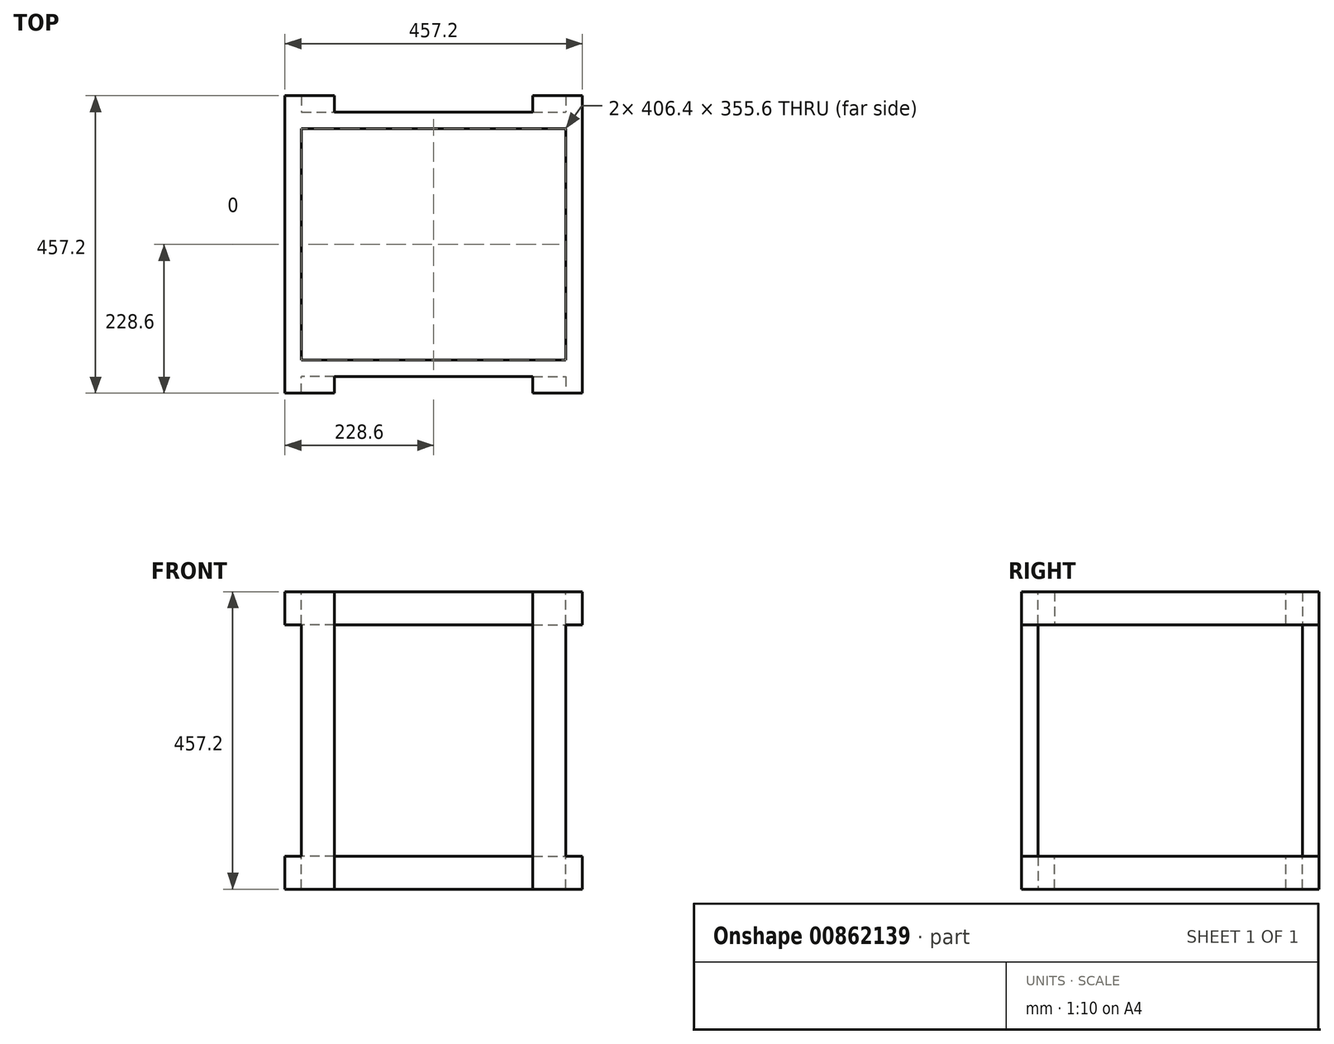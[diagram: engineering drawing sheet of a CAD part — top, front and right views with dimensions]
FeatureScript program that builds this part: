
annotation { "Feature Type Name" : "Feature", "Feature Type Description" : "" }
export const myFeature = defineFeature(function(context is Context, id is Id, definition is map)
    precondition{}
    {
        {
            var Q0;
            Q0=qCreatedBy(makeId("Front.planeOp"),FACE);
            var sketch = newSketch(context, id + "F0", { "sketchPlane" : qUnion([Q0])});
            skLineSegment(sketch, "E0.bottom", {"start": v(0, 0) * mm, "end": v(50.8, 0) * mm});
            skLineSegment(sketch, "E0.top", {"start": v(0, 457.2) * mm, "end": v(50.8, 457.2) * mm});
            skLineSegment(sketch, "E0.left", {"start": v(0, 0) * mm, "end": v(0, 457.2) * mm});
            skLineSegment(sketch, "E0.right", {"start": v(50.8, 0) * mm, "end": v(50.8, 457.2) * mm});
            skSolve(sketch);
        }
        {
            var Q0;
            Q0=makeQuery(id+"F0.imprint","IMPRINT",FACE,{"disambiguationData":[TD([[makeQuery(id+"F0.imprint","IMPRINT",EDGE,{"derivedFrom":sQuery(id+"F0.wireOp",EDGE,"E0.bottom")}),1.0]])]});
            extrude(context, id + "F1", {"entities" : qUnion([Q0]), "depth" : 25.4 * mm, "offsetDistance" : 25.4 * mm});
        }
        {
            var Q0;
            Q0=makeQuery(id+"F1.opExtrude","SWEPT_FACE",FACE,{"disambiguationData":[OSD([sQuery(id+"F0.wireOp",EDGE,"E0.right")])]});
            var sketch = newSketch(context, id + "F2", { "sketchPlane" : qUnion([Q0])});
            skLineSegment(sketch, "E1.bottom", {"start": v(-25.4, 457.2) * mm, "end": v(0, 457.2) * mm});
            skLineSegment(sketch, "E1.top", {"start": v(-25.4, 406.4) * mm, "end": v(0, 406.4) * mm});
            skLineSegment(sketch, "E1.left", {"start": v(-25.4, 457.2) * mm, "end": v(-25.4, 406.4) * mm});
            skLineSegment(sketch, "E1.right", {"start": v(0, 457.2) * mm, "end": v(0, 406.4) * mm});
            skSolve(sketch);
        }
        {
            var Q0;
            Q0=makeQuery(id+"F2.imprint","IMPRINT",FACE,{"disambiguationData":[TD([[makeQuery(id+"F2.imprint","IMPRINT",EDGE,{"derivedFrom":sQuery(id+"F2.wireOp",EDGE,"E1.bottom")}),-1.0]])]});
            extrude(context, id + "F3", {"entities" : qUnion([Q0]), "operationType" : NewBodyOperationType.ADD, "depth" : 25.4 * mm, "offsetDistance" : 25.4 * mm});
        }
        {
            var Q0;
            Q0=makeQuery(id+"F3.boolean.opBoolean","MERGE",FACE,{"derivedFrom":[makeQuery(id+"F1.opExtrude","CAP_FACE",FACE,{"disambiguationData":[OSD([sQuery(id+"F0.wireOp",EDGE,"E0.bottom"),sQuery(id+"F0.wireOp",EDGE,"E0.top"),sQuery(id+"F0.wireOp",EDGE,"E0.left"),sQuery(id+"F0.wireOp",EDGE,"E0.right")])],"isStart":false}),makeQuery(id+"F3.opExtrude","SWEPT_FACE",FACE,{"disambiguationData":[OSD([sQuery(id+"F2.wireOp",EDGE,"E1.left")])]})]});
            var sketch = newSketch(context, id + "F4", { "sketchPlane" : qUnion([Q0])});
            skLineSegment(sketch, "E2.bottom", {"start": v(76.2, 457.2) * mm, "end": v(50.8, 457.2) * mm});
            skLineSegment(sketch, "E2.top", {"start": v(76.2, 406.4) * mm, "end": v(50.8, 406.4) * mm});
            skLineSegment(sketch, "E2.left", {"start": v(76.2, 457.2) * mm, "end": v(76.2, 406.4) * mm});
            skLineSegment(sketch, "E2.right", {"start": v(50.8, 457.2) * mm, "end": v(50.8, 406.4) * mm});
            skSolve(sketch);
        }
        {
            var Q0;
            Q0=makeQuery(id+"F4.imprint","IMPRINT",FACE,{"disambiguationData":[TD([[makeQuery(id+"F4.imprint","IMPRINT",EDGE,{"derivedFrom":sQuery(id+"F4.wireOp",EDGE,"E2.bottom")}),-1.0]])]});
            extrude(context, id + "F5", {"entities" : qUnion([Q0]), "operationType" : NewBodyOperationType.ADD, "depth" : 431.8 * mm, "offsetDistance" : 25.4 * mm});
        }
        {
            var Q0;
            Q0=makeQuery(id+"F5.opExtrude","SWEPT_FACE",FACE,{"disambiguationData":[OSD([sQuery(id+"F4.wireOp",EDGE,"E2.right")])]});
            var sketch = newSketch(context, id + "F6", { "sketchPlane" : qUnion([Q0])});
            skLineSegment(sketch, "E3.bottom", {"start": v(457.2, 457.2) * mm, "end": v(431.8, 457.2) * mm});
            skLineSegment(sketch, "E3.top", {"start": v(457.2, 406.4) * mm, "end": v(431.8, 406.4) * mm});
            skLineSegment(sketch, "E3.left", {"start": v(457.2, 457.2) * mm, "end": v(457.2, 406.4) * mm});
            skLineSegment(sketch, "E3.right", {"start": v(431.8, 457.2) * mm, "end": v(431.8, 406.4) * mm});
            skSolve(sketch);
        }
        {
            var Q0;
            Q0=makeQuery(id+"F6.imprint","IMPRINT",FACE,{"disambiguationData":[TD([[makeQuery(id+"F6.imprint","IMPRINT",EDGE,{"derivedFrom":sQuery(id+"F6.wireOp",EDGE,"E3.bottom")}),1.0]])]});
            extrude(context, id + "F7", {"entities" : qUnion([Q0]), "operationType" : NewBodyOperationType.ADD, "depth" : 50.8 * mm, "offsetDistance" : 25.4 * mm});
        }
        {
            var Q0;
            Q0=makeQuery(id+"F7.boolean.opBoolean","MERGE",FACE,{"derivedFrom":[makeQuery(id+"F5.boolean.opBoolean","MERGE",FACE,{"derivedFrom":[makeQuery(id+"F3.opExtrude","SWEPT_FACE",FACE,{"disambiguationData":[OSD([sQuery(id+"F2.wireOp",EDGE,"E1.top")])]}),makeQuery(id+"F5.opExtrude","SWEPT_FACE",FACE,{"disambiguationData":[OSD([sQuery(id+"F4.wireOp",EDGE,"E2.top")])]})]}),makeQuery(id+"F7.opExtrude","SWEPT_FACE",FACE,{"disambiguationData":[OSD([sQuery(id+"F6.wireOp",EDGE,"E3.top")])]})]});
            var sketch = newSketch(context, id + "F8", { "sketchPlane" : qUnion([Q0])});
            skLineSegment(sketch, "E4.bottom", {"start": v(0, 431.8) * mm, "end": v(50.8, 431.8) * mm});
            skLineSegment(sketch, "E4.top", {"start": v(0, 457.2) * mm, "end": v(50.8, 457.2) * mm});
            skLineSegment(sketch, "E4.left", {"start": v(0, 431.8) * mm, "end": v(0, 457.2) * mm});
            skLineSegment(sketch, "E4.right", {"start": v(50.8, 431.8) * mm, "end": v(50.8, 457.2) * mm});
            skSolve(sketch);
        }
        {
            var Q0;
            Q0=makeQuery(id+"F8.imprint","IMPRINT",FACE,{"disambiguationData":[TD([[makeQuery(id+"F8.imprint","IMPRINT",EDGE,{"derivedFrom":sQuery(id+"F8.wireOp",EDGE,"E4.bottom")}),1.0]])]});
            extrude(context, id + "F9", {"entities" : qUnion([Q0]), "operationType" : NewBodyOperationType.ADD, "depth" : 406.4 * mm, "offsetDistance" : 25.4 * mm});
        }
        {
            var Q0;
            Q0=makeQuery(id+"F1.opExtrude","SWEPT_FACE",FACE,{"disambiguationData":[OSD([sQuery(id+"F0.wireOp",EDGE,"E0.right")])]});
            var sketch = newSketch(context, id + "F10", { "sketchPlane" : qUnion([Q0])});
            skLineSegment(sketch, "E5.bottom", {"start": v(0, 0) * mm, "end": v(-25.4, 0) * mm});
            skLineSegment(sketch, "E5.top", {"start": v(0, 50.8) * mm, "end": v(-25.4, 50.8) * mm});
            skLineSegment(sketch, "E5.left", {"start": v(0, 0) * mm, "end": v(0, 50.8) * mm});
            skLineSegment(sketch, "E5.right", {"start": v(-25.4, 0) * mm, "end": v(-25.4, 50.8) * mm});
            skSolve(sketch);
        }
        {
            var Q0;
            Q0=makeQuery(id+"F10.imprint","IMPRINT",FACE,{"disambiguationData":[TD([[makeQuery(id+"F10.imprint","IMPRINT",EDGE,{"derivedFrom":sQuery(id+"F10.wireOp",EDGE,"E5.bottom")}),1.0]])]});
            extrude(context, id + "F11", {"entities" : qUnion([Q0]), "operationType" : NewBodyOperationType.ADD, "depth" : 25.4 * mm, "offsetDistance" : 25.4 * mm});
        }
        {
            var Q0;
            Q0=makeQuery(id+"F11.boolean.opBoolean","MERGE",FACE,{"derivedFrom":[makeQuery(id+"F3.boolean.opBoolean","MERGE",FACE,{"derivedFrom":[makeQuery(id+"F1.opExtrude","CAP_FACE",FACE,{"disambiguationData":[OSD([sQuery(id+"F0.wireOp",EDGE,"E0.bottom"),sQuery(id+"F0.wireOp",EDGE,"E0.top"),sQuery(id+"F0.wireOp",EDGE,"E0.left"),sQuery(id+"F0.wireOp",EDGE,"E0.right")])],"isStart":false}),makeQuery(id+"F3.opExtrude","SWEPT_FACE",FACE,{"disambiguationData":[OSD([sQuery(id+"F2.wireOp",EDGE,"E1.left")])]})]}),makeQuery(id+"F11.opExtrude","SWEPT_FACE",FACE,{"disambiguationData":[OSD([sQuery(id+"F10.wireOp",EDGE,"E5.right")])]})]});
            var sketch = newSketch(context, id + "F12", { "sketchPlane" : qUnion([Q0])});
            skLineSegment(sketch, "E6.bottom", {"start": v(76.2, 0) * mm, "end": v(50.8, 0) * mm});
            skLineSegment(sketch, "E6.top", {"start": v(76.2, 50.8) * mm, "end": v(50.8, 50.8) * mm});
            skLineSegment(sketch, "E6.left", {"start": v(76.2, 0) * mm, "end": v(76.2, 50.8) * mm});
            skLineSegment(sketch, "E6.right", {"start": v(50.8, 0) * mm, "end": v(50.8, 50.8) * mm});
            skSolve(sketch);
        }
        {
            var Q0;
            Q0=makeQuery(id+"F12.imprint","IMPRINT",FACE,{"disambiguationData":[TD([[makeQuery(id+"F12.imprint","IMPRINT",EDGE,{"derivedFrom":sQuery(id+"F12.wireOp",EDGE,"E6.bottom")}),1.0]])]});
            extrude(context, id + "F13", {"entities" : qUnion([Q0]), "operationType" : NewBodyOperationType.ADD, "depth" : 431.8 * mm, "offsetDistance" : 25.4 * mm});
        }
        {
            var Q0;
            Q0=makeQuery(id+"F9.boolean.opBoolean","MERGE",FACE,{"derivedFrom":[makeQuery(id+"F7.opExtrude","SWEPT_FACE",FACE,{"disambiguationData":[OSD([sQuery(id+"F6.wireOp",EDGE,"E3.right")])]}),makeQuery(id+"F9.opExtrude","SWEPT_FACE",FACE,{"disambiguationData":[OSD([sQuery(id+"F8.wireOp",EDGE,"E4.bottom")])]})]});
            var sketch = newSketch(context, id + "F14", { "sketchPlane" : qUnion([Q0])});
            skLineSegment(sketch, "E7.bottom", {"start": v(-50.8, 457.2) * mm, "end": v(0, 457.2) * mm});
            skLineSegment(sketch, "E7.top", {"start": v(-50.8, 406.4) * mm, "end": v(0, 406.4) * mm});
            skLineSegment(sketch, "E7.left", {"start": v(-50.8, 457.2) * mm, "end": v(-50.8, 406.4) * mm});
            skLineSegment(sketch, "E7.right", {"start": v(0, 457.2) * mm, "end": v(0, 406.4) * mm});
            skSolve(sketch);
        }
        {
            var Q0;
            Q0=makeQuery(id+"F14.imprint","IMPRINT",FACE,{"disambiguationData":[TD([[makeQuery(id+"F14.imprint","IMPRINT",EDGE,{"derivedFrom":sQuery(id+"F14.wireOp",EDGE,"E7.bottom")}),1.0]])]});
            extrude(context, id + "F15", {"entities" : qUnion([Q0]), "operationType" : NewBodyOperationType.ADD, "depth" : 25.4 * mm, "offsetDistance" : 25.4 * mm});
        }
        {
            var Q0;
            Q0=makeQuery(id+"F15.boolean.opBoolean","MERGE",FACE,{"derivedFrom":[makeQuery(id+"F9.boolean.opBoolean","MERGE",FACE,{"derivedFrom":[makeQuery(id+"F7.opExtrude","CAP_FACE",FACE,{"disambiguationData":[OSD([sQuery(id+"F6.wireOp",EDGE,"E3.bottom"),sQuery(id+"F6.wireOp",EDGE,"E3.top"),sQuery(id+"F6.wireOp",EDGE,"E3.left"),sQuery(id+"F6.wireOp",EDGE,"E3.right")])],"isStart":false}),makeQuery(id+"F9.opExtrude","SWEPT_FACE",FACE,{"disambiguationData":[OSD([sQuery(id+"F8.wireOp",EDGE,"E4.left")])]})]}),makeQuery(id+"F15.opExtrude","SWEPT_FACE",FACE,{"disambiguationData":[OSD([sQuery(id+"F14.wireOp",EDGE,"E7.right")])]})]});
            var sketch = newSketch(context, id + "F16", { "sketchPlane" : qUnion([Q0])});
            skLineSegment(sketch, "E8.bottom", {"start": v(406.4, 406.4) * mm, "end": v(431.8, 406.4) * mm});
            skLineSegment(sketch, "E8.top", {"start": v(406.4, 457.2) * mm, "end": v(431.8, 457.2) * mm});
            skLineSegment(sketch, "E8.left", {"start": v(406.4, 406.4) * mm, "end": v(406.4, 457.2) * mm});
            skLineSegment(sketch, "E8.right", {"start": v(431.8, 406.4) * mm, "end": v(431.8, 457.2) * mm});
            skSolve(sketch);
        }
        {
            var Q0;
            Q0 = qSketchRegion(id + "F16", true);
            extrude(context, id + "F17", {"entities" : qUnion([Q0]), "operationType" : NewBodyOperationType.ADD, "depth" : 381 * mm, "offsetDistance" : 25.4 * mm});
        }
        {
            var Q0;
            Q0=makeQuery(id+"F17.opExtrude","SWEPT_FACE",FACE,{"disambiguationData":[OSD([sQuery(id+"F16.wireOp",EDGE,"E8.right")])]});
            var sketch = newSketch(context, id + "F18", { "sketchPlane" : qUnion([Q0])});
            skLineSegment(sketch, "E9.bottom", {"start": v(-381, 457.2) * mm, "end": v(-304.8, 457.2) * mm});
            skLineSegment(sketch, "E9.top", {"start": v(-381, 406.4) * mm, "end": v(-304.8, 406.4) * mm});
            skLineSegment(sketch, "E9.left", {"start": v(-381, 457.2) * mm, "end": v(-381, 406.4) * mm});
            skLineSegment(sketch, "E9.right", {"start": v(-304.8, 457.2) * mm, "end": v(-304.8, 406.4) * mm});
            skSolve(sketch);
        }
        {
            var Q0;
            Q0=makeQuery(id+"F18.imprint","IMPRINT",FACE,{"disambiguationData":[TD([[makeQuery(id+"F18.imprint","IMPRINT",EDGE,{"derivedFrom":sQuery(id+"F18.wireOp",EDGE,"E9.bottom")}),-1.0]])]});
            extrude(context, id + "F19", {"entities" : qUnion([Q0]), "operationType" : NewBodyOperationType.ADD, "depth" : 25.4 * mm, "offsetDistance" : 25.4 * mm});
        }
        {
            var Q0;
            Q0=makeQuery(id+"F19.boolean.opBoolean","MERGE",FACE,{"derivedFrom":[makeQuery(id+"F17.boolean.opBoolean","MERGE",FACE,{"derivedFrom":[makeQuery(id+"F15.boolean.opBoolean","MERGE",FACE,{"derivedFrom":[makeQuery(id+"F7.boolean.opBoolean","MERGE",FACE,{"derivedFrom":[makeQuery(id+"F5.boolean.opBoolean","MERGE",FACE,{"derivedFrom":[makeQuery(id+"F3.opExtrude","SWEPT_FACE",FACE,{"disambiguationData":[OSD([sQuery(id+"F2.wireOp",EDGE,"E1.top")])]}),makeQuery(id+"F5.opExtrude","SWEPT_FACE",FACE,{"disambiguationData":[OSD([sQuery(id+"F4.wireOp",EDGE,"E2.top")])]})]}),makeQuery(id+"F7.opExtrude","SWEPT_FACE",FACE,{"disambiguationData":[OSD([sQuery(id+"F6.wireOp",EDGE,"E3.top")])]})]}),makeQuery(id+"F15.opExtrude","SWEPT_FACE",FACE,{"disambiguationData":[OSD([sQuery(id+"F14.wireOp",EDGE,"E7.top")])]})]}),makeQuery(id+"F17.opExtrude","SWEPT_FACE",FACE,{"disambiguationData":[OSD([sQuery(id+"F16.wireOp",EDGE,"E8.bottom")])]})]}),makeQuery(id+"F19.opExtrude","SWEPT_FACE",FACE,{"disambiguationData":[OSD([sQuery(id+"F18.wireOp",EDGE,"E9.top")])]})]});
            var sketch = newSketch(context, id + "F20", { "sketchPlane" : qUnion([Q0])});
            skLineSegment(sketch, "E10.bottom", {"start": v(-304.8, 457.2) * mm, "end": v(-355.6, 457.2) * mm});
            skLineSegment(sketch, "E10.top", {"start": v(-304.8, 431.8) * mm, "end": v(-355.6, 431.8) * mm});
            skLineSegment(sketch, "E10.left", {"start": v(-304.8, 457.2) * mm, "end": v(-304.8, 431.8) * mm});
            skLineSegment(sketch, "E10.right", {"start": v(-355.6, 457.2) * mm, "end": v(-355.6, 431.8) * mm});
            skSolve(sketch);
        }
        {
            var Q0;
            Q0=makeQuery(id+"F20.imprint","IMPRINT",FACE,{"disambiguationData":[TD([[makeQuery(id+"F20.imprint","IMPRINT",EDGE,{"derivedFrom":sQuery(id+"F20.wireOp",EDGE,"E10.bottom")}),-1.0]])]});
            extrude(context, id + "F21", {"entities" : qUnion([Q0]), "operationType" : NewBodyOperationType.ADD, "depth" : 406.4 * mm, "offsetDistance" : 25.4 * mm});
        }
        {
            var Q0;
            Q0=makeQuery(id+"F17.boolean.opBoolean","MERGE",FACE,{"derivedFrom":[makeQuery(id+"F15.opExtrude","CAP_FACE",FACE,{"disambiguationData":[OSD([sQuery(id+"F14.wireOp",EDGE,"E7.bottom"),sQuery(id+"F14.wireOp",EDGE,"E7.top"),sQuery(id+"F14.wireOp",EDGE,"E7.left"),sQuery(id+"F14.wireOp",EDGE,"E7.right")])],"isStart":false}),makeQuery(id+"F17.opExtrude","SWEPT_FACE",FACE,{"disambiguationData":[OSD([sQuery(id+"F16.wireOp",EDGE,"E8.left")])]})]});
            var sketch = newSketch(context, id + "F22", { "sketchPlane" : qUnion([Q0])});
            skLineSegment(sketch, "E11.bottom", {"start": v(381, 406.4) * mm, "end": v(355.6, 406.4) * mm});
            skLineSegment(sketch, "E11.top", {"start": v(381, 457.2) * mm, "end": v(355.6, 457.2) * mm});
            skLineSegment(sketch, "E11.left", {"start": v(381, 406.4) * mm, "end": v(381, 457.2) * mm});
            skLineSegment(sketch, "E11.right", {"start": v(355.6, 406.4) * mm, "end": v(355.6, 457.2) * mm});
            skSolve(sketch);
        }
        {
            var Q0;
            Q0=makeQuery(id+"F22.imprint","IMPRINT",FACE,{"disambiguationData":[TD([[makeQuery(id+"F22.imprint","IMPRINT",EDGE,{"derivedFrom":sQuery(id+"F22.wireOp",EDGE,"E11.bottom")}),1.0]])]});
            extrude(context, id + "F23", {"entities" : qUnion([Q0]), "operationType" : NewBodyOperationType.ADD, "depth" : 406.4 * mm, "offsetDistance" : 25.4 * mm});
        }
        {
            var Q0;
            Q0=makeQuery(id+"F13.opExtrude","SWEPT_FACE",FACE,{"disambiguationData":[OSD([sQuery(id+"F12.wireOp",EDGE,"E6.right")])]});
            var sketch = newSketch(context, id + "F24", { "sketchPlane" : qUnion([Q0])});
            skLineSegment(sketch, "E12.bottom", {"start": v(431.8, 0) * mm, "end": v(406.4, 0) * mm});
            skLineSegment(sketch, "E12.top", {"start": v(431.8, 50.8) * mm, "end": v(406.4, 50.8) * mm});
            skLineSegment(sketch, "E12.left", {"start": v(431.8, 0) * mm, "end": v(431.8, 50.8) * mm});
            skLineSegment(sketch, "E12.right", {"start": v(406.4, 0) * mm, "end": v(406.4, 50.8) * mm});
            skSolve(sketch);
        }
        {
            var Q0;
            Q0=makeQuery(id+"F24.imprint","IMPRINT",FACE,{"disambiguationData":[TD([[makeQuery(id+"F24.imprint","IMPRINT",EDGE,{"derivedFrom":sQuery(id+"F24.wireOp",EDGE,"E12.bottom")}),-1.0]])]});
            extrude(context, id + "F25", {"entities" : qUnion([Q0]), "operationType" : NewBodyOperationType.ADD, "depth" : 431.8 * mm, "offsetDistance" : 25.4 * mm});
        }
        {
            var Q0;
            Q0=makeQuery(id+"F25.opExtrude","SWEPT_FACE",FACE,{"disambiguationData":[OSD([sQuery(id+"F24.wireOp",EDGE,"E12.right")])]});
            var sketch = newSketch(context, id + "F26", { "sketchPlane" : qUnion([Q0])});
            skLineSegment(sketch, "E13.bottom", {"start": v(381, 0) * mm, "end": v(355.6, 0) * mm});
            skLineSegment(sketch, "E13.top", {"start": v(381, 50.8) * mm, "end": v(355.6, 50.8) * mm});
            skLineSegment(sketch, "E13.left", {"start": v(381, 0) * mm, "end": v(381, 50.8) * mm});
            skLineSegment(sketch, "E13.right", {"start": v(355.6, 0) * mm, "end": v(355.6, 50.8) * mm});
            skSolve(sketch);
        }
        {
            var Q0;
            Q0=makeQuery(id+"F26.imprint","IMPRINT",FACE,{"disambiguationData":[TD([[makeQuery(id+"F26.imprint","IMPRINT",EDGE,{"derivedFrom":sQuery(id+"F26.wireOp",EDGE,"E13.bottom")}),-1.0]])]});
            extrude(context, id + "F27", {"entities" : qUnion([Q0]), "operationType" : NewBodyOperationType.ADD, "depth" : 406.4 * mm, "offsetDistance" : 25.4 * mm});
        }
        {
            var Q0;
            Q0=makeQuery(id+"F21.opExtrude","SWEPT_FACE",FACE,{"disambiguationData":[OSD([sQuery(id+"F20.wireOp",EDGE,"E10.right")])]});
            var sketch = newSketch(context, id + "F28", { "sketchPlane" : qUnion([Q0])});
            skLineSegment(sketch, "E14.bottom", {"start": v(457.2, 0) * mm, "end": v(431.8, 0) * mm});
            skLineSegment(sketch, "E14.top", {"start": v(457.2, 50.8) * mm, "end": v(431.8, 50.8) * mm});
            skLineSegment(sketch, "E14.left", {"start": v(457.2, 0) * mm, "end": v(457.2, 50.8) * mm});
            skLineSegment(sketch, "E14.right", {"start": v(431.8, 0) * mm, "end": v(431.8, 50.8) * mm});
            skSolve(sketch);
        }
        {
            var Q0;
            Q0=makeQuery(id+"F28.imprint","IMPRINT",FACE,{"disambiguationData":[TD([[makeQuery(id+"F28.imprint","IMPRINT",EDGE,{"derivedFrom":sQuery(id+"F28.wireOp",EDGE,"E14.bottom")}),-1.0]])]});
            extrude(context, id + "F29", {"entities" : qUnion([Q0]), "operationType" : NewBodyOperationType.ADD, "depth" : 25.4 * mm, "offsetDistance" : 25.4 * mm});
        }
        {
            var Q0;
            Q0=makeQuery(id+"F13.opExtrude","SWEPT_FACE",FACE,{"disambiguationData":[OSD([sQuery(id+"F12.wireOp",EDGE,"E6.right")])]});
            var sketch = newSketch(context, id + "F30", { "sketchPlane" : qUnion([Q0])});
            skLineSegment(sketch, "E15.bottom", {"start": v(25.4, 0) * mm, "end": v(50.8, 0) * mm});
            skLineSegment(sketch, "E15.top", {"start": v(25.4, 50.8) * mm, "end": v(50.8, 50.8) * mm});
            skLineSegment(sketch, "E15.left", {"start": v(25.4, 0) * mm, "end": v(25.4, 50.8) * mm});
            skLineSegment(sketch, "E15.right", {"start": v(50.8, 0) * mm, "end": v(50.8, 50.8) * mm});
            skSolve(sketch);
        }
        {
            var Q0;
            Q0 = qSketchRegion(id + "F30", true);
            extrude(context, id + "F31", {"entities" : qUnion([Q0]), "operationType" : NewBodyOperationType.ADD, "depth" : 431.8 * mm, "offsetDistance" : 25.4 * mm});
        }
        {
            var Q0;
            Q0=makeQuery(id+"F5.opExtrude","SWEPT_FACE",FACE,{"disambiguationData":[OSD([sQuery(id+"F4.wireOp",EDGE,"E2.right")])]});
            var sketch = newSketch(context, id + "F32", { "sketchPlane" : qUnion([Q0])});
            skLineSegment(sketch, "E16.bottom", {"start": v(25.4, 406.4) * mm, "end": v(50.8, 406.4) * mm});
            skLineSegment(sketch, "E16.top", {"start": v(25.4, 457.2) * mm, "end": v(50.8, 457.2) * mm});
            skLineSegment(sketch, "E16.left", {"start": v(25.4, 406.4) * mm, "end": v(25.4, 457.2) * mm});
            skLineSegment(sketch, "E16.right", {"start": v(50.8, 406.4) * mm, "end": v(50.8, 457.2) * mm});
            skSolve(sketch);
        }
        {
            var Q0;
            Q0=makeQuery(id+"F32.imprint","IMPRINT",FACE,{"disambiguationData":[TD([[makeQuery(id+"F32.imprint","IMPRINT",EDGE,{"derivedFrom":sQuery(id+"F32.wireOp",EDGE,"E16.bottom")}),-1.0]])]});
            extrude(context, id + "F33", {"entities" : qUnion([Q0]), "operationType" : NewBodyOperationType.ADD, "depth" : 431.8 * mm, "offsetDistance" : 25.4 * mm});
        }
        {
            var Q0;
            Q0=makeQuery(id+"F31.opExtrude","SWEPT_FACE",FACE,{"disambiguationData":[OSD([sQuery(id+"F30.wireOp",EDGE,"E15.left")])]});
            var sketch = newSketch(context, id + "F34", { "sketchPlane" : qUnion([Q0])});
            skLineSegment(sketch, "E17.bottom", {"start": v(355.6, 0) * mm, "end": v(304.8, 0) * mm});
            skLineSegment(sketch, "E17.top", {"start": v(355.6, 50.8) * mm, "end": v(304.8, 50.8) * mm});
            skLineSegment(sketch, "E17.left", {"start": v(355.6, 0) * mm, "end": v(355.6, 50.8) * mm});
            skLineSegment(sketch, "E17.right", {"start": v(304.8, 0) * mm, "end": v(304.8, 50.8) * mm});
            skSolve(sketch);
        }
        {
            var Q0;
            Q0=makeQuery(id+"F34.imprint","IMPRINT",FACE,{"disambiguationData":[TD([[makeQuery(id+"F34.imprint","IMPRINT",EDGE,{"derivedFrom":sQuery(id+"F34.wireOp",EDGE,"E17.bottom")}),-1.0]])]});
            extrude(context, id + "F35", {"entities" : qUnion([Q0]), "operationType" : NewBodyOperationType.ADD, "depth" : 25.4 * mm, "offsetDistance" : 25.4 * mm});
        }
        {
            var Q0;
            Q0=makeQuery(id+"F35.boolean.opBoolean","MERGE",FACE,{"derivedFrom":[makeQuery(id+"F31.boolean.opBoolean","MERGE",FACE,{"derivedFrom":[makeQuery(id+"F29.boolean.opBoolean","MERGE",FACE,{"derivedFrom":[makeQuery(id+"F27.boolean.opBoolean","MERGE",FACE,{"derivedFrom":[makeQuery(id+"F25.boolean.opBoolean","MERGE",FACE,{"derivedFrom":[makeQuery(id+"F13.boolean.opBoolean","MERGE",FACE,{"derivedFrom":[makeQuery(id+"F11.opExtrude","SWEPT_FACE",FACE,{"disambiguationData":[OSD([sQuery(id+"F10.wireOp",EDGE,"E5.top")])]}),makeQuery(id+"F13.opExtrude","SWEPT_FACE",FACE,{"disambiguationData":[OSD([sQuery(id+"F12.wireOp",EDGE,"E6.top")])]})]}),makeQuery(id+"F25.opExtrude","SWEPT_FACE",FACE,{"disambiguationData":[OSD([sQuery(id+"F24.wireOp",EDGE,"E12.top")])]})]}),makeQuery(id+"F27.opExtrude","SWEPT_FACE",FACE,{"disambiguationData":[OSD([sQuery(id+"F26.wireOp",EDGE,"E13.top")])]})]}),makeQuery(id+"F29.opExtrude","SWEPT_FACE",FACE,{"disambiguationData":[OSD([sQuery(id+"F28.wireOp",EDGE,"E14.top")])]})]}),makeQuery(id+"F31.opExtrude","SWEPT_FACE",FACE,{"disambiguationData":[OSD([sQuery(id+"F30.wireOp",EDGE,"E15.top")])]})]}),makeQuery(id+"F35.opExtrude","SWEPT_FACE",FACE,{"disambiguationData":[OSD([sQuery(id+"F34.wireOp",EDGE,"E17.top")])]})]});
            var sketch = newSketch(context, id + "F36", { "sketchPlane" : qUnion([Q0])});
            skLineSegment(sketch, "E18.bottom", {"start": v(-304.8, 0) * mm, "end": v(-355.6, 0) * mm});
            skLineSegment(sketch, "E18.top", {"start": v(-304.8, -25.4) * mm, "end": v(-355.6, -25.4) * mm});
            skLineSegment(sketch, "E18.left", {"start": v(-304.8, 0) * mm, "end": v(-304.8, -25.4) * mm});
            skLineSegment(sketch, "E18.right", {"start": v(-355.6, 0) * mm, "end": v(-355.6, -25.4) * mm});
            skSolve(sketch);
        }
        {
            var Q0;
            Q0=makeQuery(id+"F36.imprint","IMPRINT",FACE,{"disambiguationData":[TD([[makeQuery(id+"F36.imprint","IMPRINT",EDGE,{"derivedFrom":sQuery(id+"F36.wireOp",EDGE,"E18.bottom")}),-1.0]])]});
            extrude(context, id + "F37", {"entities" : qUnion([Q0]), "operationType" : NewBodyOperationType.ADD, "depth" : 406.4 * mm, "offsetDistance" : 25.4 * mm});
        }
    });
